# Revit family: Remeha E-HP AW 44 Ace
name_source: partatom
category: Mechanical Equipment
units: mm (PartAtom-declared; Revit-internal decimal feet)

## family parameters
Always vertical = Yes
Classification = Pump
Cut with Voids When Loaded = No
OmniClass Number = 23.75.10.21
OmniClass Title = Heat Pumps
Part Type = Normal
Room Calculation Point = No
Round Connector Dimension = Use Diameter
Shared = No
Work Plane-Based = No

## types (1)
- E-HP AW 44 Ace
    6 Monthly = 05-31
    Access Clearance Bottom = 0 mm  [stored 0 ft]
    Access Clearance Front = 2000 mm  [stored 6.56168 ft]
    Access Clearance Left = 1500 mm  [stored 4.92126 ft]
    Access Clearance Rear = 2000 mm  [stored 6.56168 ft]
    Access Clearance Right = 1500 mm  [stored 4.92126 ft]
    Access Clearance Top = 0 mm  [stored 0 ft]
    Airflow Rate (m3/min) = 128.6667
    Annually = 05-31
    Article Description = Heat pump outdoor unit
    Article Type = E-HP AW 44 Ace
    BMS Links = Yes
    Back Clearance = 2000 mm  [stored 6.56168 ft]
    Base Family Version = 11.19
    Bespoke Timeframe = 0
    Black = Color RGB 060-060-060
    Bottom Clearance = 0 mm  [stored 0 ft]
    CE Mark = Yes
    Coefficient of Performance = 4.6
    Colour = IGP Dura Pol (Brand Colour)
    Condensate Drain Size = 0 mm  [stored 0 ft]
    Configuration = Single Unit
    Content Supplier URL = www.MEPcontent.com
    Control Options = Modulating
    Control Type = Weather Compensation, 0-10V, Time Control, DHW Control.
    Cooling EER (kW/kW) = 0
    Cooling Power Input (kW) = 0
    Custom = No
    Daily = 0
    Default Elevation = 0 mm  [stored 0 ft]
    Depth = 769 mm  [stored 2.52297 ft]
    Description = Heat pump outdoor unit
    Drain Connection Size = 32 mm  [stored 0.104987 ft]
    Drain Connection Type = Other
    Drain Diameter = 32 mm  [stored 0.104987 ft]
    Drain Fixture Units = 0
    EMCS Version = 4.0
    ETIM Article Class = EC001213
    Embodied Carbon = 0
    ErP Energy Label = A++
    Expected Life = 0
    External Material = Steel
    Family Version = 11.19
    Features = The Remeha E-HP AW can be used in projects ranging from small light commercial properties to multi-valent energy centres for large commercial buildings
    Finish = Galvanised & Powder Coated
    Flow and Return Connection Size = 40 mm  [stored 0.131234 ft]
    Flow and Return Connection Type = Threaded
    Frequency = 50 Hz
    Front Clearance = 2000 mm  [stored 6.56168 ft]
    Full Load Current = 27 A
    Fuse Rating = 0 A
    Global Warming Potential of Refrigerant = 1774
    Grey = Color RGB 150-153-146
    Gross Weight = 460.00 kg
    Heat Exchanger Material = Stainless Steel
    Heating COP (kW/kW) = 4.6
    Heating Power Input (kW) = 34.1
    Height = 2095.5 mm  [stored 6.875 ft]
    Hertz = 50 Hz
    Hydronic Return Diameter = 38.1 mm
    Hydronic Supply Diameter = 38.1 mm
    IP Rating Electrical Enclosure = IP42
    IfcExportAs = IfcHeatExchangerType
    IfcExportType = NOTDEFINED
    Interlocks = Yes
    Left Clearance = 1500 mm  [stored 4.92126 ft]
    Life Cycle Analysis = 0
    MEPcontent Class = HEATPUMP
    Manufacturer = Remeha
    Manufacturer Art. No. = 7681851
    Mass of Refrigerant = 14.00 kg
    Maximum Air Flow Rate = 0
    Maximum Air Temperature for Cylinder Charging only = 20
    Maximum Air Temperature for Heating only = 20
    Maximum DHW Flow Temperature = 20
    Maximum Heating Operating Pressure = 3200000.0 Pa
    Maximum Heating Output = 34300 W
    Maximum Heating Water Flow Rate = 1.6 L/s
    Maximum Operating Pressure of Refrigerant = 3500000.0 Pa
    Maximum Power Consumption = 7700 W
    Minimum Air Temperature for Heating and Cylinder Charging = -20
    Minimum Heating Operating Pressure = 0.0 Pa
    Minimum Heating Water Flow Rate = 0.8 L/s
    Minimum Operating Pressure of Refrigerant = 0.0 Pa
    Model = E-HP AW 44 Ace
    Monthly = 0
    Mounting = Floor Standing
    Nominal Diameter = 38.1 mm
    Outer Diameter = 48.3 mm  [stored 0.158465 ft]
    Overall Height = 2100 mm
    Overall Length = 1206 mm
    Overall Width = 688 mm
    Phase = 3
    Product Line = E-HP AW
    Product Literature = https://www.remeha.co.uk
    Product Range = E-HP AW 44 Ace
    Quarterly = 0
    Rated Current = 0 A
    Reference Standard = Machine directive 2006/42/EC, Low tension directive 2006/95/EC, EMC directive 2004/108/EC, Pressure Equipment directive 97/23/EWG
    Refrigerant Type = R407C
    Refrigeration Circuit Type = Single Circuit
    Revit Version = 2018
    Right Clearance = 1500 mm  [stored 4.92126 ft]
    Safety Valve Connection Size = 0 mm  [stored 0 ft]
    Seasonal Coefficient of Performance = 4.09
    Seasonal Space Heating Efficiency = 160
    Shape = Rectangular (Vertical)
    Shipping Weight = 0.00 kg
    Sound Power Level for A7W35 = 65
    Sound Pressure Level (dB(A)) = 65
    Starting Current = 96 A
    Supply Phase = 0
    Top Clearance = 500 mm  [stored 1.64042 ft]
    Type = Monoblock
    URL = www.stabiplan.com
    Uniclass2015 = Pr_70_60_37_04
    Unit Weight (kg) = 460
    Use Nominal Diameter = Yes
    Voltage = 400 V
    Warranty ID = https://mediacdn.pottertoncommercial.co.uk
    Water Content = 0.01 m³
    Weekly = 0
    White = Color RGB 200-200-200
    Width = 1206 mm

note: [stored X ft] marks values corroborated as IEEE doubles in the binary element streams (Revit-internal decimal feet)

## geometry (parser evidence)
native form markers: Sweep x5
no freeform markers — native parametric forms only
